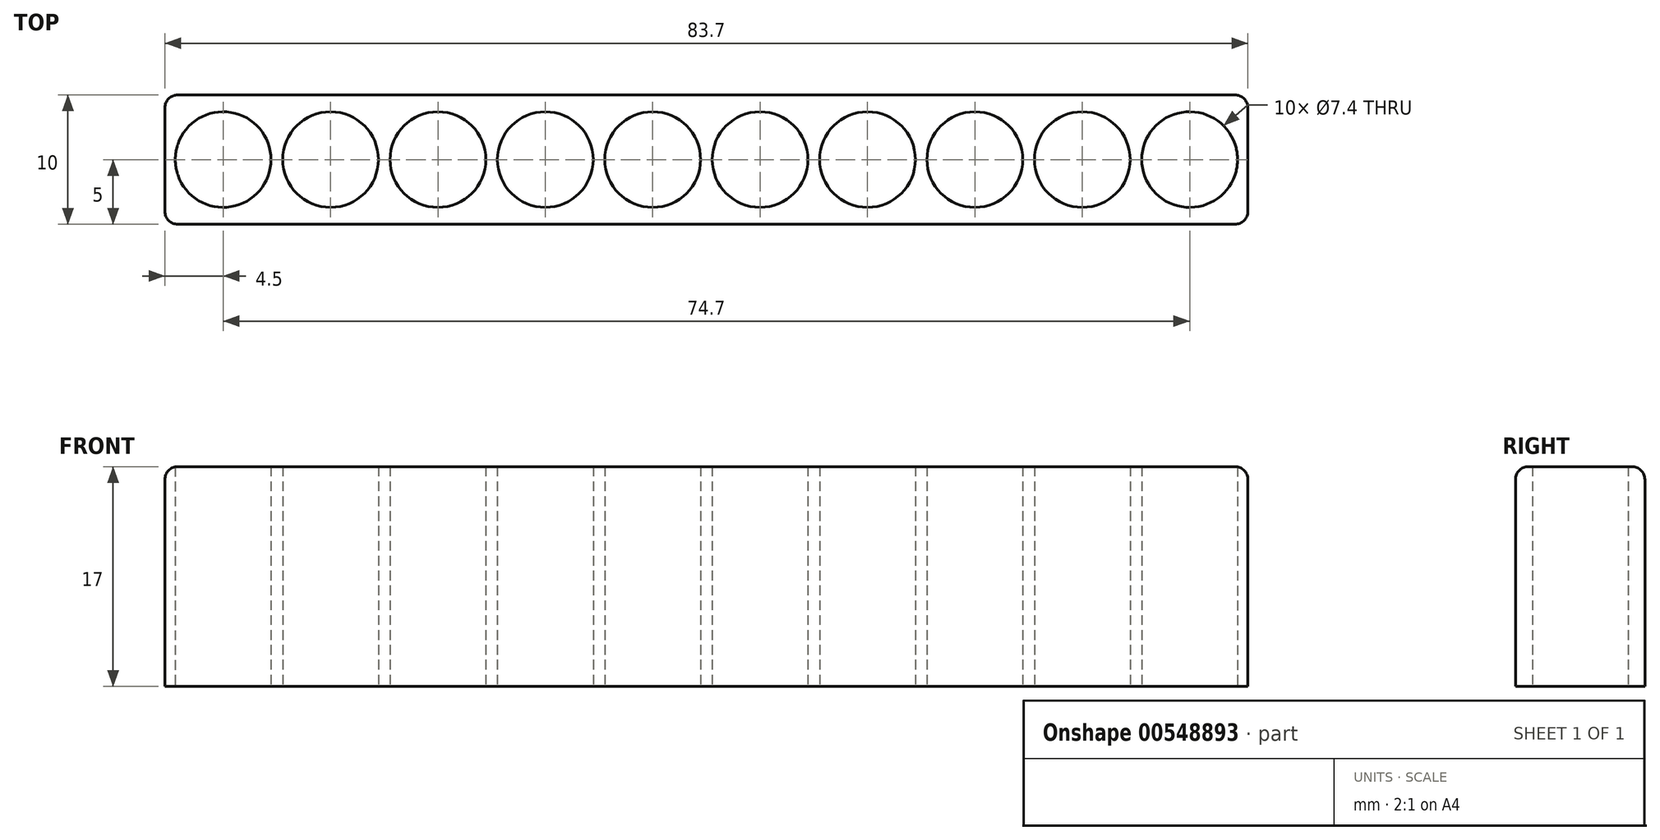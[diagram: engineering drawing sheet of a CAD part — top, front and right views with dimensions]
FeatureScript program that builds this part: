
annotation { "Feature Type Name" : "Feature", "Feature Type Description" : "" }
export const myFeature = defineFeature(function(context is Context, id is Id, definition is map)
    precondition{}
    {
        {
            var Q0;
            Q0=qCreatedBy(makeId("Top.planeOp"),FACE);
            var sketch = newSketch(context, id + "F0", { "sketchPlane" : qUnion([Q0])});
            skCircle(sketch, "E0", {"center": v(0, 0) * mm, "radius": 3.7 * mm});
            skCircle(sketch, "E1.1.0.0", {"center": v(8.3, 0) * mm, "radius": 3.7 * mm});
            skCircle(sketch, "E1.2.0.0", {"center": v(16.6, 0) * mm, "radius": 3.7 * mm});
            skCircle(sketch, "E1.3.0.0", {"center": v(24.9, 0) * mm, "radius": 3.7 * mm});
            skCircle(sketch, "E1.4.0.0", {"center": v(33.2, 0) * mm, "radius": 3.7 * mm});
            skCircle(sketch, "E1.5.0.0", {"center": v(41.5, 0) * mm, "radius": 3.7 * mm});
            skCircle(sketch, "E1.6.0.0", {"center": v(49.8, 0) * mm, "radius": 3.7 * mm});
            skCircle(sketch, "E1.7.0.0", {"center": v(58.1, 0) * mm, "radius": 3.7 * mm});
            skCircle(sketch, "E1.8.0.0", {"center": v(66.4, 0) * mm, "radius": 3.7 * mm});
            skCircle(sketch, "E1.9.0.0", {"center": v(74.7, 0) * mm, "radius": 3.7 * mm});
            skLineSegment(sketch, "E1.direction1", {"start": v(0, 0) * mm, "end": v(8.3, 0) * mm, "construction": true});
            skLineSegment(sketch, "E2.bottom", {"start": v(-3.5, -5) * mm, "end": v(78.2, -5) * mm});
            skLineSegment(sketch, "E2.top", {"start": v(-3.5, 5) * mm, "end": v(78.2, 5) * mm});
            skLineSegment(sketch, "E2.left", {"start": v(-4.5, -4) * mm, "end": v(-4.5, 4) * mm});
            skLineSegment(sketch, "E2.right", {"start": v(79.2, -4) * mm, "end": v(79.2, 4) * mm});
            skPoint(sketch, "E3.visualSharp", {"position": v(-4.5, -5) * mm});
            skArc(sketch, "E3.filletArc", {"start": v(-4.5, -4) * mm, "mid": v(-4.2, -4.7) * mm, "end": v(-3.5, -5) * mm});
            skPoint(sketch, "E4.visualSharp", {"position": v(-4.5, 5) * mm});
            skArc(sketch, "E4.filletArc", {"start": v(-3.5, 5) * mm, "mid": v(-4.2, 4.7) * mm, "end": v(-4.5, 4) * mm});
            skPoint(sketch, "E5.visualSharp", {"position": v(79.2, 5) * mm});
            skArc(sketch, "E5.filletArc", {"start": v(79.2, 4) * mm, "mid": v(78.9, 4.7) * mm, "end": v(78.2, 5) * mm});
            skPoint(sketch, "E6.visualSharp", {"position": v(79.2, -5) * mm});
            skArc(sketch, "E6.filletArc", {"start": v(78.2, -5) * mm, "mid": v(78.9, -4.7) * mm, "end": v(79.2, -4) * mm});
            skSolve(sketch);
        }
        {
            var Q0;
            Q0=makeQuery(id+"F0.imprint","IMPRINT",FACE,{"disambiguationData":[TD([[makeQuery(id+"F0.imprint","IMPRINT",EDGE,{"derivedFrom":sQuery(id+"F0.wireOp",EDGE,"E0")}),-1.0]])]});
            extrude(context, id + "F1", {"entities" : qUnion([Q0]), "depth" : 17 * mm, "offsetDistance" : 25 * mm});
        }
        {
            var Q0;
            Q0=makeQuery(id+"F1.opExtrude","CAP_EDGE",EDGE,{"disambiguationData":[OSD([sQuery(id+"F0.wireOp",EDGE,"E2.bottom")])],"isStart":false});
            var Q1;
            Q1=makeQuery(id+"F1.opExtrude","CAP_EDGE",EDGE,{"disambiguationData":[OSD([sQuery(id+"F0.wireOp",EDGE,"E2.top")])],"isStart":false});
            fillet(context, id + "F2", {"entities" : qUnion([Q0, Q1]), "radius" : 1 * mm, "tangentPropagation" : true, "allowEdgeOverflow" : false});
        }
    });
